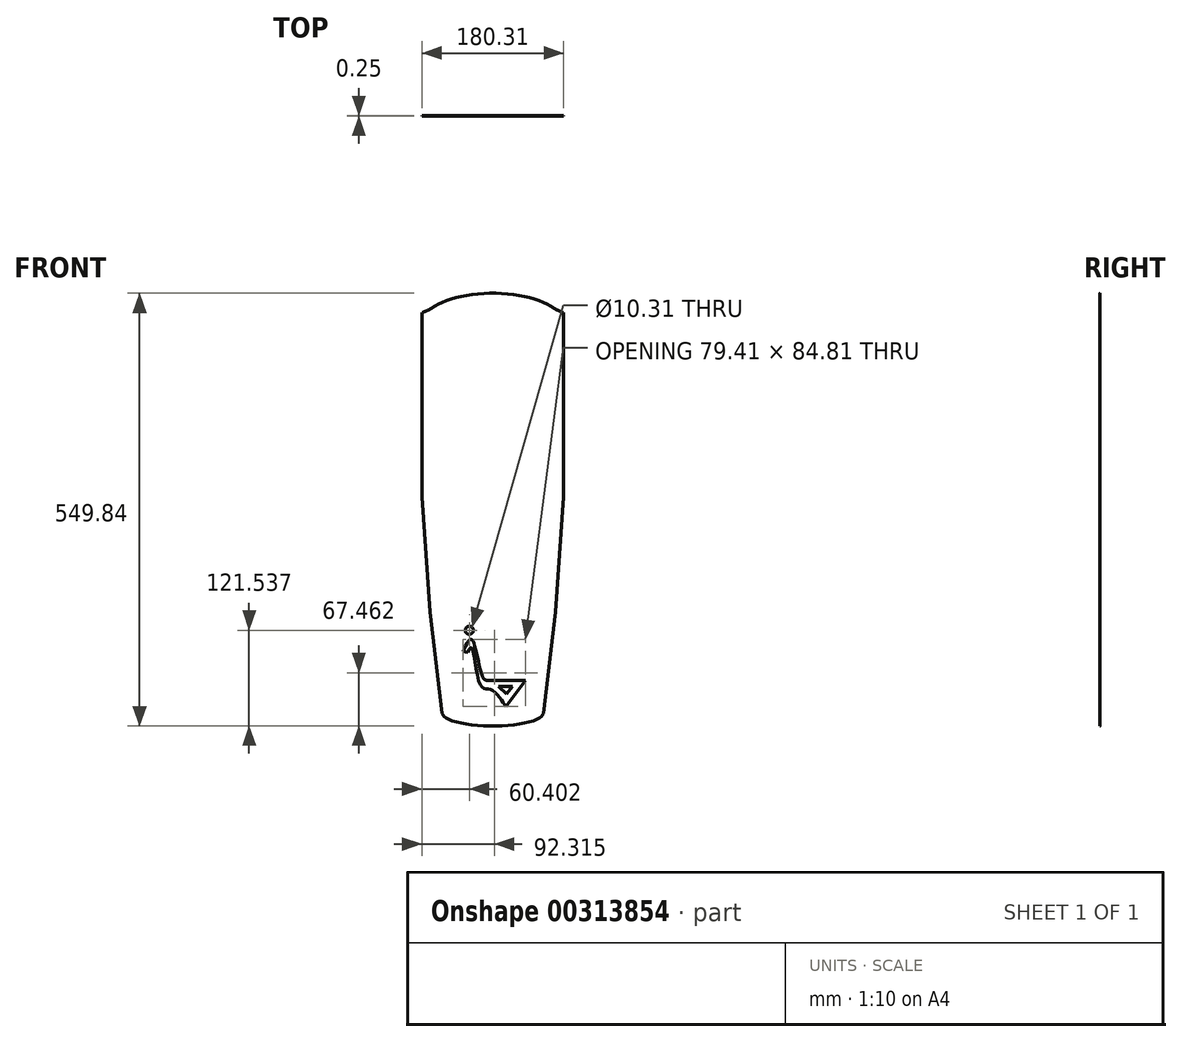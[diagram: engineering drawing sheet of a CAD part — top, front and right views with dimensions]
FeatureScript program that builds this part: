
annotation { "Feature Type Name" : "Feature", "Feature Type Description" : "" }
export const myFeature = defineFeature(function(context is Context, id is Id, definition is map)
    precondition{}
    {
        {
            var Q0;
            Q0=qCreatedBy(makeId("Front.planeOp"),FACE);
            var sketch = newSketch(context, id + "F0", { "sketchPlane" : qUnion([Q0])});
            skFitSpline(sketch, "E0", {"points": [v(-23.73, 15.59) * mm, v(-19.28, 21.52) * mm, v(-8.89, -23.38) * mm, v(-1.1, -30.43) * mm, v(6.32, -31.91) * mm, v(18.2, -43.79) * mm, v(24.5, -52.7) * mm], "startDerivative": vector(38.92, 88.04) * mm, "endDerivative": vector(37.91, -56.37) * mm});
            skLineSegment(sketch, "E1", {"start": v(24.5, -52.7) * mm, "end": v(49.74, -20.04) * mm});
            skLineSegment(sketch, "E2", {"start": v(49.74, -20.04) * mm, "end": v(0.02, -20.04) * mm});
            skFitSpline(sketch, "E3", {"points": [v(-29.67, 17.07) * mm, v(-18.9, 31.91) * mm, v(-5.92, -12.99) * mm, v(0.02, -20.04) * mm], "startDerivative": vector(37.5, 84.16) * mm, "endDerivative": vector(28.28, -15.02) * mm});
            skLineSegment(sketch, "E4", {"start": v(-29.67, 17.07) * mm, "end": v(-23.73, 15.59) * mm});
            skCircle(sketch, "E5", {"center": v(-21.88, 43.79) * mm, "radius": 5.16 * mm});
            skLineSegment(sketch, "E6", {"start": v(32.67, -27.46) * mm, "end": v(25.62, -36.74) * mm});
            skLineSegment(sketch, "E7", {"start": v(25.62, -36.74) * mm, "end": v(15.13, -27.46) * mm});
            skLineSegment(sketch, "E8", {"start": v(15.13, -27.46) * mm, "end": v(32.67, -27.46) * mm});
            skSolve(sketch);
        }
        {
            var Q0;
            Q0=qCreatedBy(makeId("Front.planeOp"),FACE);
            var sketch = newSketch(context, id + "F1", { "sketchPlane" : qUnion([Q0])});
            skCircle(sketch, "E9", {"center": v(-12.76, 490.56) * mm, "radius": 2.38 * mm});
            skCircle(sketch, "E10", {"center": v(-12.76, 554.06) * mm, "radius": 2.38 * mm});
            skCircle(sketch, "E11.MirrorC", {"center": v(28.51, 554.06) * mm, "radius": 2.38 * mm});
            skCircle(sketch, "E12.MirrorC", {"center": v(28.51, 490.56) * mm, "radius": 2.38 * mm});
            skCircle(sketch, "E13", {"center": v(28.51, -94.67) * mm, "radius": 2.38 * mm});
            skCircle(sketch, "E14", {"center": v(28.51, -158.17) * mm, "radius": 2.38 * mm});
            skCircle(sketch, "E15.MirrorC", {"center": v(-12.76, -94.67) * mm, "radius": 2.38 * mm});
            skCircle(sketch, "E16.MirrorC", {"center": v(-12.76, -158.17) * mm, "radius": 2.38 * mm});
            skLineSegment(sketch, "E17", {"start": v(7.88, 610.3) * mm, "end": v(7.88, -261.42) * mm, "construction": true});
            skLineSegment(sketch, "E18", {"start": v(101.57, 174.43) * mm, "end": v(-85.82, 174.43) * mm, "construction": true});
            skPoint(sketch, "E18.startSnap0", {"position": v(7.88, 174.43) * mm});
            skArc(sketch, "E19.0", {"start": v(98.03, 447.34) * mm, "mid": v(62.64, 473.14) * mm, "end": v(48.37, 514.54) * mm});
            skLineSegment(sketch, "E19.1", {"start": v(46.72, 574.45) * mm, "end": v(48.37, 514.54) * mm});
            skLineSegment(sketch, "E19.2", {"start": v(7.88, 610.3) * mm, "end": v(46.72, 574.45) * mm});
            skLineSegment(sketch, "E19.3", {"start": v(7.88, 610.3) * mm, "end": v(-30.96, 574.45) * mm});
            skLineSegment(sketch, "E19.4", {"start": v(-30.96, 574.45) * mm, "end": v(-32.61, 514.54) * mm});
            skLineSegment(sketch, "E19.5", {"start": v(98.03, 447.34) * mm, "end": v(98.03, 213.1) * mm});
            skArc(sketch, "E19.6", {"start": v(-82.28, 447.34) * mm, "mid": v(-46.89, 473.14) * mm, "end": v(-32.61, 514.54) * mm});
            skLineSegment(sketch, "E19.7", {"start": v(-82.28, 447.34) * mm, "end": v(-82.28, 213.1) * mm});
            skLineSegment(sketch, "E19.8", {"start": v(47.35, -107.87) * mm, "end": v(26.63, -247.54) * mm});
            skLineSegment(sketch, "E19.9", {"start": v(72.28, -61.76) * mm, "end": v(47.35, -107.87) * mm});
            skLineSegment(sketch, "E19.10", {"start": v(87.38, 67.28) * mm, "end": v(72.28, -61.76) * mm});
            skLineSegment(sketch, "E19.11", {"start": v(98.03, 213.1) * mm, "end": v(87.38, 67.28) * mm});
            skArc(sketch, "E19.12", {"start": v(26.63, -247.54) * mm, "mid": v(20.26, -259.11) * mm, "end": v(7.88, -263.72) * mm});
            skArc(sketch, "E19.13", {"start": v(-10.88, -247.54) * mm, "mid": v(-4.5, -259.11) * mm, "end": v(7.88, -263.72) * mm});
            skLineSegment(sketch, "E19.14", {"start": v(-31.6, -107.87) * mm, "end": v(-10.88, -247.54) * mm});
            skLineSegment(sketch, "E19.15", {"start": v(-56.52, -61.76) * mm, "end": v(-31.6, -107.87) * mm});
            skLineSegment(sketch, "E19.16", {"start": v(-71.63, 67.28) * mm, "end": v(-56.52, -61.76) * mm});
            skLineSegment(sketch, "E19.17", {"start": v(-82.28, 213.1) * mm, "end": v(-71.63, 67.28) * mm});
            skEllipticalArc(sketch, "E20", {});
            skEllipticalArc(sketch, "E21", {});
            const initialGuessF1  = {"E20": [0.007875822484493249, 0.4374167025089264, 0, 1, 0.03467203039726324, 0.08602920655165483, 5.262019748332322, 1.0211655588472652], "E21": [0.007875822484493264, -0.06145787239074707, 1, 0, 0.06396240535590753, 0.01629231539492421, 3.2784171397153816, 6.146360821053997]};
            skSetInitialGuess(sketch, initialGuessF1);
            skSolve(sketch);
        }
        {
            var Q0;
            {var subQ3=sQuery(id+"F1.wireOp",EDGE,"E19.5");Q0=makeQuery(id+"F1.imprint","IMPRINT",FACE,{"disambiguationData":[TD([[makeQuery(id+"F1.imprint","IMPRINT",EDGE,{"derivedFrom":subQ3}),-1.0]])]});}
            extrude(context, id + "F2", {"entities" : qUnion([Q0]), "depth" : 0.25 * mm});
        }
        {
            var Q0;
            Q0 = qSketchRegion(id + "F0", true);
            extrude(context, id + "F3", {"entities" : qUnion([Q0]), "operationType" : NewBodyOperationType.REMOVE, "depth" : 40.64 * mm});
        }
    });
